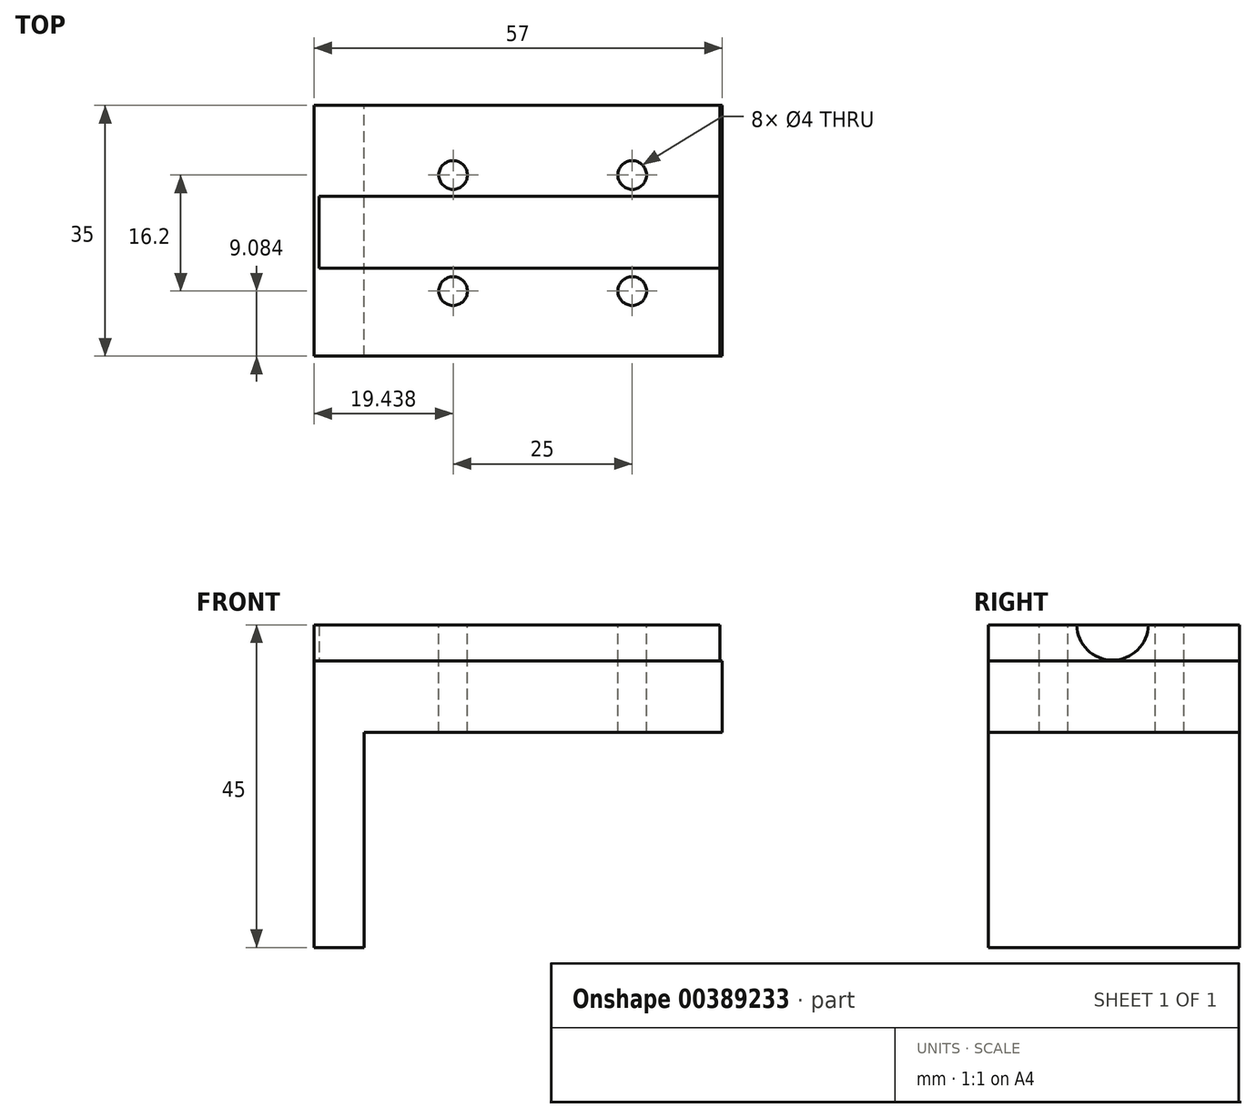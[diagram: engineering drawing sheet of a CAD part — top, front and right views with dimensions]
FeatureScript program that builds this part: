
annotation { "Feature Type Name" : "Feature", "Feature Type Description" : "" }
export const myFeature = defineFeature(function(context is Context, id is Id, definition is map)
    precondition{}
    {
        {
            var Q0;
            Q0=qCreatedBy(makeId("Front.planeOp"),FACE);
            var sketch = newSketch(context, id + "F0", { "sketchPlane" : qUnion([Q0])});
            skLineSegment(sketch, "E0", {"start": v(-51.76, 0) * mm, "end": v(-51.76, 30) * mm});
            skLineSegment(sketch, "E1", {"start": v(-51.76, 30) * mm, "end": v(-1.76, 30) * mm});
            skLineSegment(sketch, "E2.0", {"start": v(-61.76, 40) * mm, "end": v(-2.06, 40) * mm});
            skLineSegment(sketch, "E2.1", {"start": v(-61.76, 0) * mm, "end": v(-61.76, 40) * mm});
            skLineSegment(sketch, "E3", {"start": v(-51.76, 0) * mm, "end": v(-61.76, 0) * mm});
            skLineSegment(sketch, "E4", {"start": v(-2.06, 40) * mm, "end": v(-1.76, 40) * mm});
            skLineSegment(sketch, "E5", {"start": v(-1.76, 40) * mm, "end": v(-1.76, 30) * mm});
            skSolve(sketch);
        }
        {
            var Q0;
            Q0=makeQuery(id+"F0.imprint","IMPRINT",FACE,{"disambiguationData":[TD([[makeQuery(id+"F0.imprint","IMPRINT",EDGE,{"derivedFrom":sQuery(id+"F0.wireOp",EDGE,"E0")}),1.0]])]});
            extrude(context, id + "F1", {"entities" : qUnion([Q0]), "depth" : 35 * mm});
        }
        {
            var Q0;
            Q0=makeQuery(id+"F1.opExtrude","SWEPT_FACE",FACE,{"disambiguationData":[OSD([sQuery(id+"F0.wireOp",EDGE,"E2.0")])]});
            extrude(context, id + "F2", {"entities" : qUnion([Q0]), "depth" : 5 * mm});
        }
        {
            var Q0;
            Q0=makeQuery(id+"F2.opExtrude","SWEPT_FACE",FACE,{"disambiguationData":[OSD([sQuery(id+"F0.wireOp",EDGE,"E2.0"),sQuery(id+"F0.wireOp",EDGE,"E4")])]});
            var sketch = newSketch(context, id + "F3", { "sketchPlane" : qUnion([Q0])});
            skCircle(sketch, "E6", {"center": v(-17.7, 45.1) * mm, "radius": 5 * mm});
            skSolve(sketch);
        }
        {
            var Q0;
            Q0=qSketchRegion(id+"F3",true);
            extrude(context, id + "F4", {"entities" : qUnion([Q0]), "operationType" : NewBodyOperationType.REMOVE, "oppositeDirection" : true, "depth" : 56 * mm});
        }
        {
            var Q0;
            {var subQ0=sQuery(id+"F0.wireOp",EDGE,"E2.0");Q0=makeQuery(id+"F4.boolean.opBoolean","SPLIT",FACE,{"disambiguationData":[TD([makeQuery(id+"F2.opExtrude","SWEPT_FACE",FACE,{"disambiguationData":[OSD([subQ0]),TDD([makeQuery(id+"F1.opExtrude","CAP_EDGE",EDGE,{"disambiguationData":[OSD([subQ0])],"isStart":true})])]})])],"derivedFrom":makeQuery(id+"F2.opExtrude","CAP_FACE",FACE,{"disambiguationData":[OSD([subQ0])],"isStart":false})});}
            var sketch = newSketch(context, id + "F5", { "sketchPlane" : qUnion([Q0])});
            skCircle(sketch, "E7", {"center": v(-39.32, -25.92) * mm, "radius": 2 * mm});
            skCircle(sketch, "E8.0.1.0", {"center": v(-39.32, -9.72) * mm, "radius": 2 * mm});
            skCircle(sketch, "E8.1.0.0", {"center": v(-14.32, -25.92) * mm, "radius": 2 * mm});
            skCircle(sketch, "E8.1.1.0", {"center": v(-14.32, -9.72) * mm, "radius": 2 * mm});
            skLineSegment(sketch, "E8.direction1", {"start": v(-39.32, -25.92) * mm, "end": v(-14.32, -25.92) * mm, "construction": true});
            skLineSegment(sketch, "E8.direction2", {"start": v(-39.32, -25.92) * mm, "end": v(-39.32, -9.72) * mm, "construction": true});
            skSolve(sketch);
        }
        {
            var Q0;
            Q0=makeQuery(id+"F5.imprint","IMPRINT",FACE,{"disambiguationData":[TD([[makeQuery(id+"F5.imprint","IMPRINT",EDGE,{"derivedFrom":sQuery(id+"F5.wireOp",EDGE,"E8.0.1.0")}),1.0]])]});
            var Q1;
            Q1=makeQuery(id+"F5.imprint","IMPRINT",FACE,{"disambiguationData":[TD([[makeQuery(id+"F5.imprint","IMPRINT",EDGE,{"derivedFrom":sQuery(id+"F5.wireOp",EDGE,"E8.1.1.0")}),1.0]])]});
            var Q2;
            Q2=makeQuery(id+"F5.imprint","IMPRINT",FACE,{"disambiguationData":[TD([[makeQuery(id+"F5.imprint","IMPRINT",EDGE,{"derivedFrom":sQuery(id+"F5.wireOp",EDGE,"E8.1.0.0")}),1.0]])]});
            var Q3;
            Q3=makeQuery(id+"F5.imprint","IMPRINT",FACE,{"disambiguationData":[TD([[makeQuery(id+"F5.imprint","IMPRINT",EDGE,{"derivedFrom":sQuery(id+"F5.wireOp",EDGE,"E7")}),1.0]])]});
            var Q4;
            Q4=sQuery(id+"F5.wireOp",EDGE,"E8.0.1.0");
            var Q5;
            Q5=sQuery(id+"F5.wireOp",EDGE,"E8.1.1.0");
            var Q6;
            Q6=sQuery(id+"F5.wireOp",EDGE,"E8.1.0.0");
            var Q7;
            Q7=sQuery(id+"F5.wireOp",EDGE,"E7");
            extrude(context, id + "F6", {"entities" : qUnion([Q0, Q1, Q2, Q3]), "operationType" : NewBodyOperationType.REMOVE, "surfaceEntities" : qUnion([Q4, Q5, Q6, Q7]), "endBound" : BoundingType.THROUGH_ALL, "oppositeDirection" : true, "depth" : 25 * mm});
        }
        {
            var Q0;
            Q0=makeQuery(id+"F2.opExtrude","SWEPT_FACE",FACE,{"disambiguationData":[OSD([sQuery(id+"F0.wireOp",EDGE,"E2.0"),sQuery(id+"F0.wireOp",EDGE,"E2.1")])]});
            var Q1;
            Q1=makeQuery(id+"F1.opExtrude","SWEPT_FACE",FACE,{"disambiguationData":[OSD([sQuery(id+"F0.wireOp",EDGE,"E2.1")])]});
            extrude(context, id + "F7", {"entities" : qUnion([Q0, Q1]), "operationType" : NewBodyOperationType.REMOVE, "oppositeDirection" : true, "depth" : 3 * mm});
        }
    });
